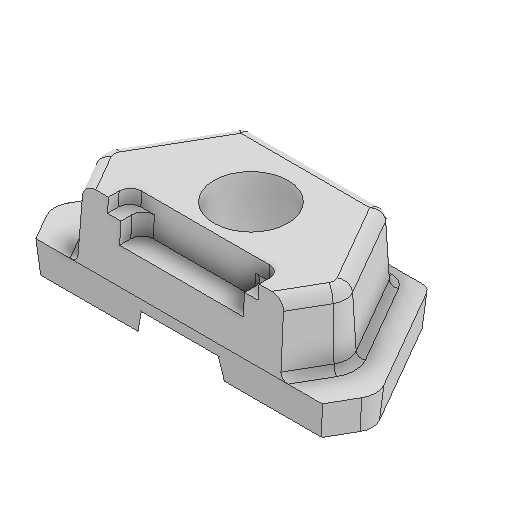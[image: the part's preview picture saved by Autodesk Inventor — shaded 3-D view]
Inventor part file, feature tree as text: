
AUTODESK INVENTOR PART (.ipt)
format: ipt  version: 2022 (Build 260153000, 153)  size: 203,776 bytes
history: native  units: in
note: dims shown in document units (in); Inventor stores cm internally (conversion verified against a paired STEP export)
features: fillet x1
ambient origin geometry x8: Origin, YZ Plane, XZ Plane, XY Plane, X Axis, Y Axis, Z Axis, Center Point
bodies: Solid1 (feature_tree)
feature tree (1):
  fillet  "Fillet8"  [1 undecoded]
note: 1 required parameter value undecoded (feature->parameter linkage not recoverable at this tier; creation-order binding heuristic only, values carry confidence <= 0.55)
